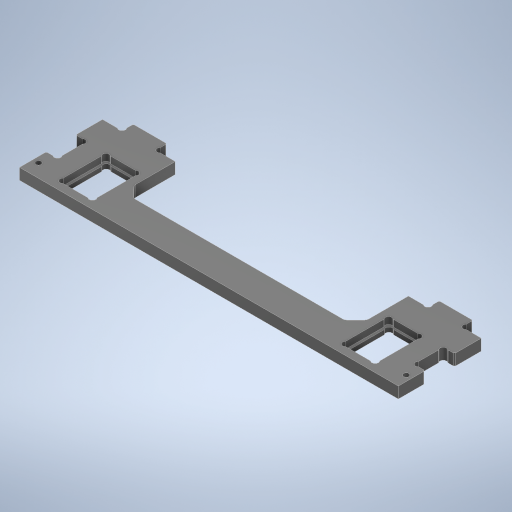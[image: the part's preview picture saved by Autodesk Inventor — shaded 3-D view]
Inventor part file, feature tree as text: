
AUTODESK INVENTOR PART (.ipt)
format: ipt  version: 2024.2 (Build 282272000, 272)  size: 461,312 bytes
history: native  units: mm
features: plane x3, extrude x2, sketch x1, hole x1, chamfer x1
ambient origin geometry x8: Origin, YZ Plane, XZ Plane, XY Plane, X Axis, Y Axis, Z Axis, Center Point
bodies: Solid1 (feature_tree)
feature tree (8):
  sketch  "Sketch1"  dims[d0=5.0mm d1=5.0mm d2=1.5mm d4=15.0mm d5=0.05mm d6=12.0mm d7=169.0mm d8=37.0mm d9=6.0mm d10=5.0mm d11=0.0mm d12=2.5mm d13=6.0mm d14=4.8mm d15=2.5mm d16=90.0deg d17=8.0mm d18=0.0mm d22=23.0mm d28=19.2mm d29=12.9mm d30=21.1mm d31=15.1mm d32=0.05mm d33=1.5mm d34=1.5mm d35=0.05mm d36=0.05mm d37=0.05mm d38=3.0mm d39=0.0mm d41=0.5mm d42=2.0mm d43=45.0deg d44=3.5mm d46=3.5mm d52=13.5mm d53=0.5mm d54=103.0mm d55=0.5mm d56=5.0mm d57=2.0mm d58=45.0deg d59=2.0mm d60=22.5mm]
  extrude  "Extrusion1"  Depth=5.0mm
  extrude  "Extrusion2"  Depth=1.5mm
  hole  "Phi2.5"  [1 undecoded]
  chamfer  "C0.5"  Distance=0.05mm
  plane  "Work Plane1"
  plane  "Work Plane2"
  plane  "Work Plane3"
note: 1 required parameter value undecoded (feature->parameter linkage not recoverable at this tier; creation-order binding heuristic only, values carry confidence <= 0.55)
